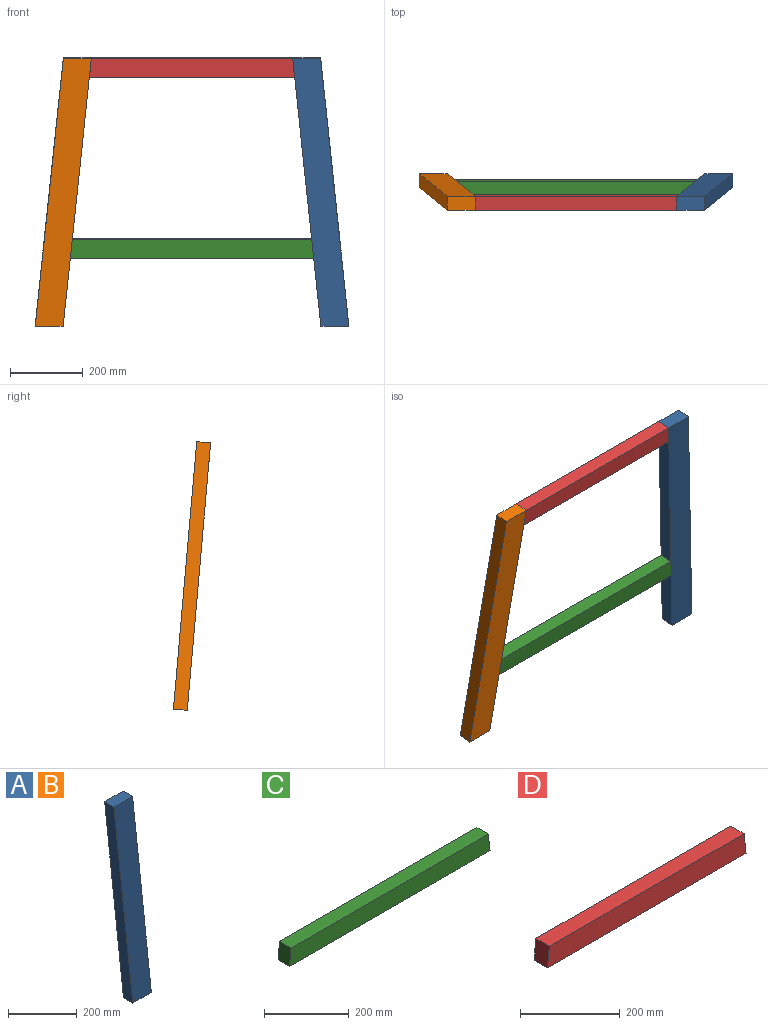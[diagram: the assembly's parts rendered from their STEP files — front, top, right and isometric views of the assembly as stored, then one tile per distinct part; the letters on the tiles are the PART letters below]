
ASSEMBLY  parts=4 mates=5
PART A: 6 faces, bbox 154x38.1x736.6 mm
  f0: plane 76.62x38.1mm, normal (0,0,1), area 2919.2mm2, adj f1,f3,f4,f5
  f1: plane 736.6x77.42mm, normal (-0.99,0,-0.1), area 28219mm2, adj f0,f2,f4,f5
  f2: plane 76.62x38.1mm, normal (0,0,-1), area 2919.2mm2, adj f1,f3,f4,f5
  f3: plane 736.6x77.42mm, normal (0.99,0,0.1), area 28219mm2, adj f0,f2,f4,f5
  f4: plane 736.6x154.04mm, normal (0,-1,0), area 56438.1mm2, adj f0,f1,f2,f3
  f5: plane 736.6x154.04mm, normal (0,1,0), area 56438.1mm2, adj f0,f1,f2,f3
PART B: same geometry as A
PART C: 6 faces, bbox 667.9x38.1x50.8 mm
  f0: plane 657.23x38.1mm, normal (0,0,1), area 25040.3mm2, adj f1,f3,f4,f5
  f1: plane 50.8x38.1mm, normal (-0.99,0,0.1), area 1946.1mm2, adj f0,f2,f4,f5
  f2: plane 667.9x38.1mm, normal (0,0,-1), area 25447.1mm2, adj f1,f3,f4,f5
  f3: plane 50.8x38.1mm, normal (0.99,0,0.1), area 1946.1mm2, adj f0,f2,f4,f5
  f4: plane 667.9x50.8mm, normal (0,-1,0), area 33658.3mm2, adj f0,f1,f2,f3
  f5: plane 667.9x50.8mm, normal (0,1,0), area 33658.3mm2, adj f0,f1,f2,f3
PART D: 6 faces, bbox 563.1x38.1x50.8 mm
  f0: plane 552.45x38.1mm, normal (0,0,1), area 21048.3mm2, adj f1,f3,f4,f5
  f1: plane 50.8x38.1mm, normal (-0.99,0,0.1), area 1946.1mm2, adj f0,f2,f4,f5
  f2: plane 563.13x38.1mm, normal (0,0,-1), area 21455.2mm2, adj f1,f3,f4,f5
  f3: plane 50.8x38.1mm, normal (0.99,0,0.1), area 1946.1mm2, adj f0,f2,f4,f5
  f4: plane 563.13x50.8mm, normal (0,-1,0), area 28335.7mm2, adj f0,f1,f2,f3
  f5: plane 563.13x50.8mm, normal (0,1,0), area 28335.7mm2, adj f0,f1,f2,f3
PLACE A rot(axis=(1,0,0),5deg) t=(337.56,101.95,-72.96)mm
PLACE B rot(axis=(0,-0.04,1),180deg) t=(-214.89,64,-76.28)mm
PLACE C rot(axis=(1,0,0),5deg) t=(-267.27,145.39,-569.5)mm
PLACE D rot(axis=(1,0,0),5deg) t=(-214.89,101.95,-72.96)mm
MATE planar C.f4 <-> A.f4  axis (0,-1,-0.09) through (61.34,109.66,-598.19)mm
MATE planar C.f3 <-> A.f1  axis (0.99,-0.01,0.1) through (392.62,128.63,-596.46)mm
MATE fastened B.f1 <-> D.f1  axis (0.99,0.01,-0.1) through (-214.89,82.97,-74.62)mm
MATE planar B.f1 <-> C.f1  axis (0.99,0.01,-0.1) through (-253.6,115.07,-441.52)mm
MATE fastened D.f3 <-> A.f1  axis (0.99,-0.01,0.1) through (337.56,82.97,-74.62)mm
